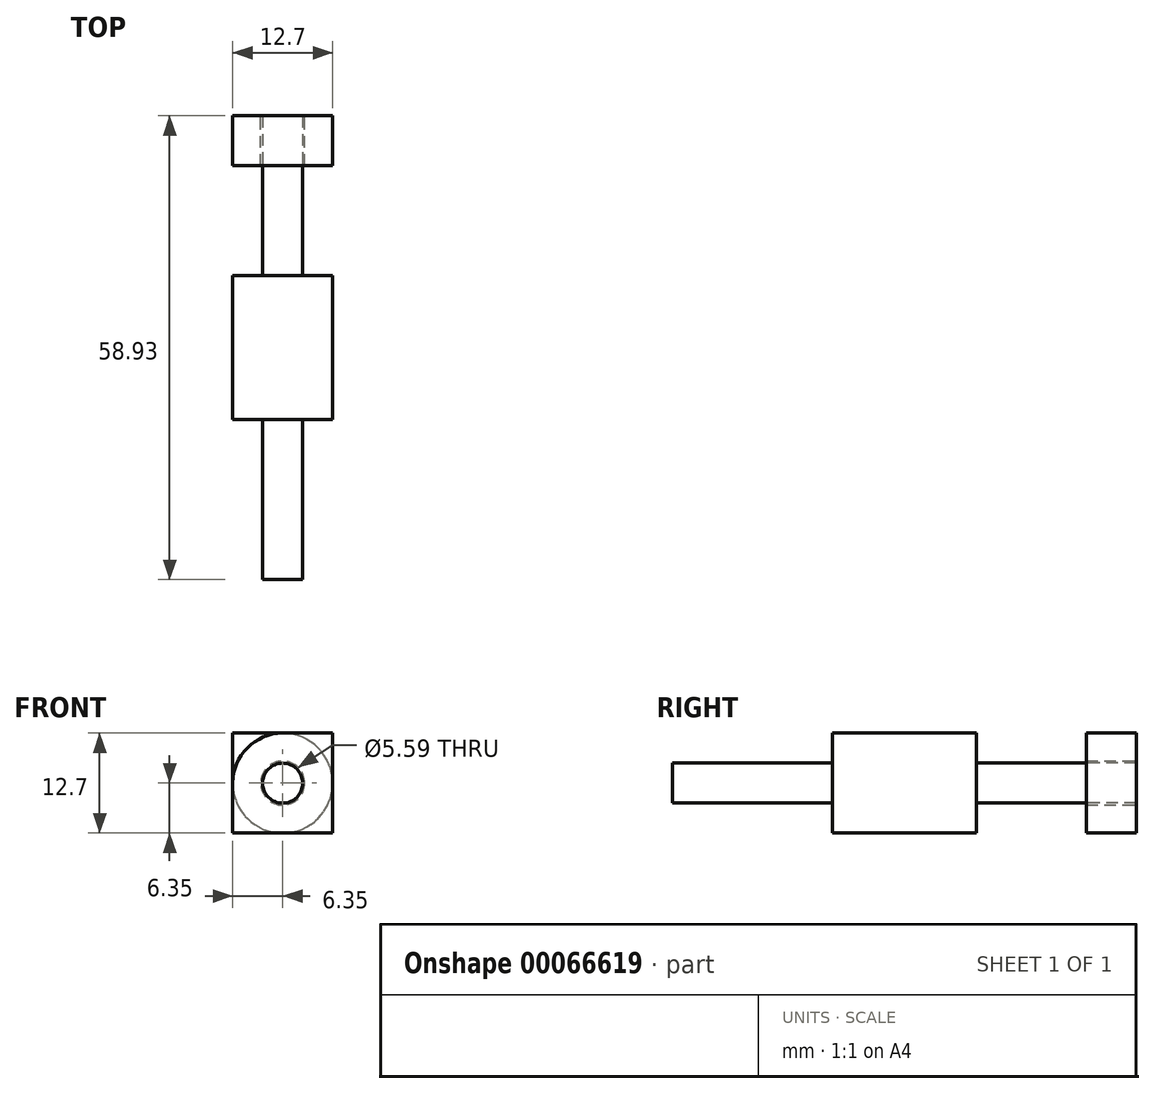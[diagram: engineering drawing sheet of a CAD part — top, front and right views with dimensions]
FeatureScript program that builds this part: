
annotation { "Feature Type Name" : "Feature", "Feature Type Description" : "" }
export const myFeature = defineFeature(function(context is Context, id is Id, definition is map)
    precondition{}
    {
        {
            var Q0;
            Q0=qCreatedBy(makeId("Front.planeOp"),FACE);
            var sketch = newSketch(context, id + "F0", { "sketchPlane" : qUnion([Q0])});
            skLineSegment(sketch, "E0.bottom", {"start": v(-6.35, 6.35) * mm, "end": v(6.35, 6.35) * mm});
            skLineSegment(sketch, "E0.top", {"start": v(-6.35, -6.35) * mm, "end": v(6.35, -6.35) * mm});
            skLineSegment(sketch, "E0.left", {"start": v(-6.35, 6.35) * mm, "end": v(-6.35, -6.35) * mm});
            skLineSegment(sketch, "E0.right", {"start": v(6.35, 6.35) * mm, "end": v(6.35, -6.35) * mm});
            skSolve(sketch);
        }
        {
            var Q0;
            Q0=qSketchRegion(id+"F0",true);
            extrude(context, id + "F1", {"entities" : qUnion([Q0]), "depth" : 18.29 * mm});
        }
        {
            var Q0;
            Q0=makeQuery(id+"F1.opExtrude","CAP_FACE",FACE,{"disambiguationData":[OSD([sQuery(id+"F0.wireOp",EDGE,"E0.bottom"),sQuery(id+"F0.wireOp",EDGE,"E0.top"),sQuery(id+"F0.wireOp",EDGE,"E0.left"),sQuery(id+"F0.wireOp",EDGE,"E0.right")])],"isStart":true});
            var sketch = newSketch(context, id + "F2", { "sketchPlane" : qUnion([Q0])});
            skCircle(sketch, "E1", {"center": v(0, 0) * mm, "radius": 2.54 * mm});
            skSolve(sketch);
        }
        {
            var Q0;
            Q0=qSketchRegion(id+"F2",true);
            extrude(context, id + "F3", {"entities" : qUnion([Q0]), "operationType" : NewBodyOperationType.ADD, "depth" : 20.32 * mm});
        }
        {
            var Q0;
            Q0=makeQuery(id+"F1.opExtrude","CAP_FACE",FACE,{"disambiguationData":[OSD([sQuery(id+"F0.wireOp",EDGE,"E0.bottom"),sQuery(id+"F0.wireOp",EDGE,"E0.top"),sQuery(id+"F0.wireOp",EDGE,"E0.left"),sQuery(id+"F0.wireOp",EDGE,"E0.right")])],"isStart":false});
            var sketch = newSketch(context, id + "F4", { "sketchPlane" : qUnion([Q0])});
            skCircle(sketch, "E2", {"center": v(0, 0) * mm, "radius": 2.54 * mm});
            skSolve(sketch);
        }
        {
            var Q0;
            Q0=qSketchRegion(id+"F4",true);
            extrude(context, id + "F5", {"entities" : qUnion([Q0]), "operationType" : NewBodyOperationType.ADD, "depth" : 20.32 * mm});
        }
        {
            var Q0;
            Q0=makeQuery(id+"F3.opExtrude","CAP_FACE",FACE,{"disambiguationData":[OSD([sQuery(id+"F2.wireOp",EDGE,"E1")])],"isStart":false});
            var sketch = newSketch(context, id + "F6", { "sketchPlane" : qUnion([Q0])});
            skCircle(sketch, "E3", {"center": v(0, 0) * mm, "radius": 6.35 * mm});
            skCircle(sketch, "E4", {"center": v(0, 0) * mm, "radius": 2.8 * mm});
            skSolve(sketch);
        }
        {
            var Q0;
            Q0=qSketchRegion(id+"F6",true);
            extrude(context, id + "F7", {"entities" : qUnion([Q0]), "oppositeDirection" : true, "depth" : 6.35 * mm});
        }
    });
